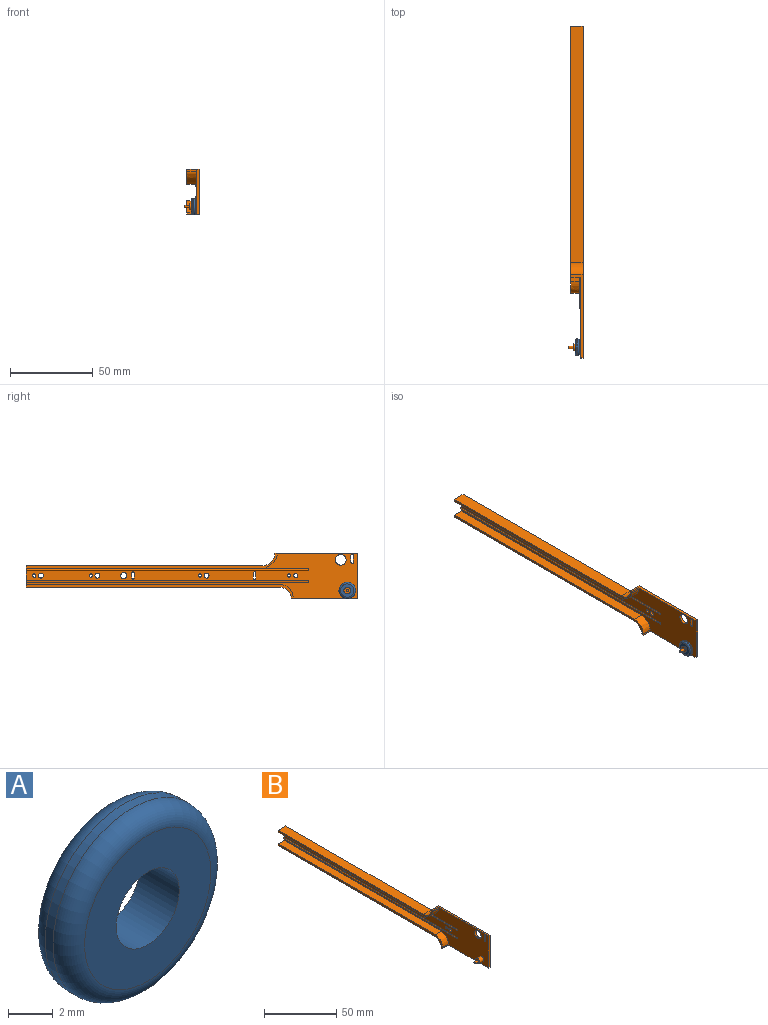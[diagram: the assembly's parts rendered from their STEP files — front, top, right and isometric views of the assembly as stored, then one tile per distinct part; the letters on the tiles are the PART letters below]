
ASSEMBLY  parts=2 mates=1
PART A: 6 faces, bbox 10.8x2.5x10.8 mm
  f0: cylinder r=5mm len=10mm, axis (0,1,0), area 15.7mm2, adj f3,f4
  f1: plane 8x8mm, normal (0,-1,0), area 37.7mm2, adj f3,f5
  f2: plane 8x8mm, normal (0,1,0), area 37.7mm2, adj f4,f5
  f3: torus R=4mm, axis (0,-1,0), area 45.8mm2, adj f0,f1
  f4: torus R=4mm, axis (0,-1,0), area 45.8mm2, adj f0,f2
  f5: cylinder r=2mm len=4mm, axis (0,-1,0), area 31.4mm2, adj f1,f2
PART B: 48 faces, bbox 8.5x200x27.3 mm
  f0: plane 200x27.25mm, normal (1,0,0), area 3165.4mm2, adj f6,f7,f9,f10,f11,f14,f15,f16
  f1: plane 200x27.25mm, normal (-1,0,0), area 2335.7mm2, adj f3,f4,f6,f7,f8,f9,f12,f13
  f2: plane 151.26x9mm, normal (-1,0,0), area 229.9mm2, adj f3,f6,f10,f14,f15,f19,f21
  f3: plane 143.95x6mm, normal (0,0,-1), area 863.7mm2, adj f1,f2,f14,f21
  f4: plane 6x1mm, normal (0,-1,0), area 6mm2, adj f1,f5,f7,f20
  f5: plane 160.89x8.25mm, normal (-1,0,0), area 247.2mm2, adj f4,f7,f8,f11,f14,f16,f20
  f6: plane 50x7.5mm, normal (0,0,1), area 82.6mm2, adj f0,f1,f2,f9,f15,f19
  f7: plane 40x7.5mm, normal (0,0,-1), area 65.3mm2, adj f0,f1,f4,f5,f9,f16
  f8: plane 153.77x6mm, normal (0,0,1), area 922.6mm2, adj f1,f5,f14,f20
  f9: plane 27.25x1.5mm, normal (0,-1,0), area 40.9mm2, adj f0,f1,f6,f7
  f10: plane 142.5x7.5mm, normal (0,0,1), area 1068.8mm2, adj f0,f2,f14,f15
  f11: plane 152.54x7.5mm, normal (0,0,-1), area 1144mm2, adj f0,f5,f14,f16
  f12: cylinder r=0.5mm len=170mm, axis (0,-1,0), area 267mm2, adj f1,f14,f17
  f13: cylinder r=0.5mm len=170mm, axis (0,-1,0), area 267mm2, adj f1,f14,f18
  f14: plane 13x7.5mm, normal (0,1,0), area 38.3mm2, adj f0,f1,f2,f3,f5,f8,f10,f11
  f15: cylinder r=7.5mm len=7.5mm, axis (1,0,0), area 88.4mm2, adj f0,f2,f6,f10
  f16: cylinder r=7.5mm len=7.5mm, axis (-1,0,0), area 82.7mm2, adj f0,f5,f7,f11
  f17: plane 1x0.5mm, normal (0,-1,0), area 0.4mm2, adj f1,f12
  f18: plane 1x0.5mm, normal (0,-1,0), area 0.4mm2, adj f1,f13
  f19: plane 6x1.18mm, normal (0,-1,0), area 7.1mm2, adj f1,f2,f6,f21
  f20: extruded ~7.25x7.12mm, area 67mm2, adj f1,f4,f5,f8
  f21: extruded ~7.83x7.32mm, area 67.4mm2, adj f1,f2,f3,f19
  f22: cylinder r=2mm len=4mm, axis (1,0,0), area 50.3mm2, adj f1,f23
  f23: plane 4x4mm, normal (-1,0,0), area 10.8mm2, adj f22,f25
  f24: plane 1.5x1.5mm, normal (-1,0,0), area 1.8mm2, adj f25
  f25: cylinder r=0.75mm len=3mm, axis (1,0,0), area 14.1mm2, adj f23,f24
  f26: cylinder r=1.5mm len=3mm, axis (-1,0,0), area 14.1mm2, adj f0,f1
  f27: cylinder r=1mm len=2mm, axis (-1,0,0), area 9.4mm2, adj f0,f1
  f28: cylinder r=1.25mm len=2.5mm, axis (-1,0,0), area 11.8mm2, adj f0,f1
  f29: cylinder r=1.9mm len=3.8mm, axis (-1,0,0), area 17.9mm2, adj f0,f1
  f30: cylinder r=1mm len=2mm, axis (-1,0,0), area 9.4mm2, adj f0,f1
  f31: cylinder r=1.5mm len=3mm, axis (-1,0,0), area 14.1mm2, adj f0,f1
  f32: cylinder r=1mm len=2mm, axis (-1,0,0), area 9.4mm2, adj f0,f1
  f33: cylinder r=1.5mm len=3mm, axis (-1,0,0), area 14.1mm2, adj f0,f1
  f34: cylinder r=0.75mm len=1.5mm, axis (-1,0,0), area 3.5mm2, adj f0,f1,f35,f37
  f35: plane 4x1.5mm, normal (0,-1,0), area 6mm2, adj f0,f1,f34,f36
  f36: cylinder r=0.75mm len=1.5mm, axis (-1,0,0), area 3.5mm2, adj f0,f1,f35,f37
  f37: plane 4x1.5mm, normal (0,1,0), area 6mm2, adj f0,f1,f34,f36
  f38: cylinder r=0.75mm len=1.5mm, axis (-1,0,0), area 3.5mm2, adj f0,f1,f39,f41
  f39: plane 3x1.5mm, normal (0,-1,0), area 4.5mm2, adj f0,f1,f38,f40
  f40: cylinder r=0.75mm len=1.5mm, axis (-1,0,0), area 3.5mm2, adj f0,f1,f39,f41
  f41: plane 3x1.5mm, normal (0,1,0), area 4.5mm2, adj f0,f1,f38,f40
  f42: cylinder r=0.75mm len=1.5mm, axis (-1,0,0), area 3.5mm2, adj f0,f1,f43,f45
  f43: plane 3x1.5mm, normal (0,-1,0), area 4.5mm2, adj f0,f1,f42,f44
  f44: cylinder r=0.75mm len=1.5mm, axis (-1,0,0), area 3.5mm2, adj f0,f1,f43,f45
  f45: plane 3x1.5mm, normal (0,1,0), area 4.5mm2, adj f0,f1,f42,f44
  f46: cylinder r=3.25mm len=6.5mm, axis (-1,0,0), area 30.6mm2, adj f0,f1
  f47: cylinder r=1mm len=2mm, axis (-1,0,0), area 9.4mm2, adj f0,f1
PLACE A rot(axis=(-0.58,0.58,0.58),120deg) t=(-16.97,0.54,-11.68)mm
PLACE B t=(-19.72,24.09,-9.68)mm
MATE revolute A.f5 <-> B.f25  axis (1,0,0) through (-15.72,0.54,-11.68)mm
